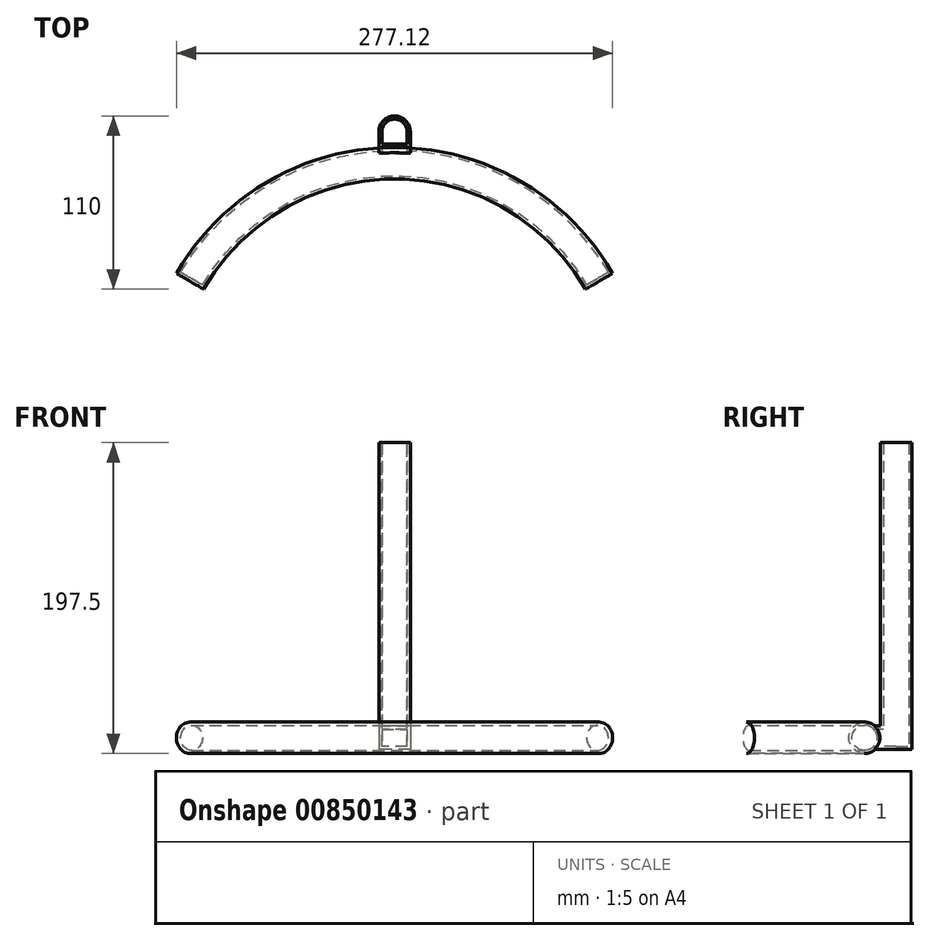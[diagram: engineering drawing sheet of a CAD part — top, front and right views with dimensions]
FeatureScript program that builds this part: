
annotation { "Feature Type Name" : "Feature", "Feature Type Description" : "" }
export const myFeature = defineFeature(function(context is Context, id is Id, definition is map)
    precondition{}
    {
        {
            var Q0;
            Q0=qCreatedBy(makeId("Right.planeOp"),FACE);
            var sketch = newSketch(context, id + "F0", { "sketchPlane" : qUnion([Q0])});
            skCircle(sketch, "E0", {"center": v(0, 0) * mm, "radius": 10 * mm});
            skLineSegment(sketch, "E1", {"start": v(-150, 26.36) * mm, "end": v(-150, -31.35) * mm});
            skSolve(sketch);
        }
        {
            var Q0;
            Q0=makeQuery(id+"F0.imprint","IMPRINT",FACE,{"disambiguationData":[TD([[makeQuery(id+"F0.imprint","IMPRINT",EDGE,{"derivedFrom":sQuery(id+"F0.wireOp",EDGE,"E0")}),1.0]])]});
            var Q1;
            Q1=sQuery(id+"F0.wireOp",EDGE,"E1");
            revolve(context, id + "F1", {"surfaceOperationType" : NewSurfaceOperationType.NEW, "entities" : qUnion([Q0]), "axis" : qUnion([Q1]), "revolveType" : RevolveType.SYMMETRIC, "angle" : 120 * degree});
        }
        {
            var Q0;
            Q0=qCreatedBy(makeId("Front.planeOp"),FACE);
            var sketch = newSketch(context, id + "F2", { "sketchPlane" : qUnion([Q0])});
            skLineSegment(sketch, "E2.bottom", {"start": v(10, 7.5) * mm, "end": v(-10, 7.5) * mm});
            skLineSegment(sketch, "E2.top", {"start": v(10, -7.5) * mm, "end": v(-10, -7.5) * mm});
            skLineSegment(sketch, "E2.left", {"start": v(10, 7.5) * mm, "end": v(10, -7.5) * mm});
            skLineSegment(sketch, "E2.right", {"start": v(-10, 7.5) * mm, "end": v(-10, -7.5) * mm});
            skSolve(sketch);
        }
        {
            var Q0;
            Q0 = qSketchRegion(id + "F2", true);
            extrude(context, id + "F3", {"entities" : qUnion([Q0]), "operationType" : NewBodyOperationType.ADD, "oppositeDirection" : true, "depth" : 30 * mm, "offsetDistance" : 25 * mm});
        }
        {
            var Q0;
            Q0=makeQuery(id+"F3.opExtrude","SWEPT_FACE",FACE,{"disambiguationData":[OSD([sQuery(id+"F2.wireOp",EDGE,"E2.bottom")])]});
            var sketch = newSketch(context, id + "F4", { "sketchPlane" : qUnion([Q0])});
            skLineSegment(sketch, "E3.bottom", {"start": v(-10, 30) * mm, "end": v(10, 30) * mm});
            skLineSegment(sketch, "E3.top", {"start": v(-10, 10) * mm, "end": v(10, 10) * mm});
            skLineSegment(sketch, "E3.left", {"start": v(-10, 30) * mm, "end": v(-10, 10) * mm});
            skLineSegment(sketch, "E3.right", {"start": v(10, 30) * mm, "end": v(10, 10) * mm});
            skSolve(sketch);
        }
        {
            var Q0;
            Q0=makeQuery(id+"F4.imprint","IMPRINT",FACE,{"disambiguationData":[TD([[makeQuery(id+"F4.imprint","IMPRINT",EDGE,{"derivedFrom":sQuery(id+"F4.wireOp",EDGE,"E3.bottom")}),1.0]])]});
            extrude(context, id + "F5", {"entities" : qUnion([Q0]), "operationType" : NewBodyOperationType.ADD, "depth" : 180 * mm, "offsetDistance" : 25 * mm});
        }
        {
            var Q0;
            Q0=makeQuery(id+"F5.boolean.opBoolean","MERGE",EDGE,{"derivedFrom":[makeQuery(id+"F3.opExtrude","CAP_EDGE",EDGE,{"disambiguationData":[OSD([sQuery(id+"F2.wireOp",EDGE,"E2.left")])],"isStart":false}),makeQuery(id+"F5.opExtrude","SWEPT_EDGE",EDGE,{"disambiguationData":[OSD([sQuery(id+"F4.wireOp",EDGE,"E3.bottom"),sQuery(id+"F4.wireOp",EDGE,"E3.right")])]})]});
            var Q1;
            Q1=makeQuery(id+"F5.boolean.opBoolean","MERGE",EDGE,{"derivedFrom":[makeQuery(id+"F3.opExtrude","CAP_EDGE",EDGE,{"disambiguationData":[OSD([sQuery(id+"F2.wireOp",EDGE,"E2.right")])],"isStart":false}),makeQuery(id+"F5.opExtrude","SWEPT_EDGE",EDGE,{"disambiguationData":[OSD([sQuery(id+"F4.wireOp",EDGE,"E3.bottom"),sQuery(id+"F4.wireOp",EDGE,"E3.left")])]})]});
            fillet(context, id + "F6", {"entities" : qUnion([Q0, Q1]), "radius" : 10 * mm, "tangentPropagation" : true, "allowEdgeOverflow" : false});
        }
        {
            var Q0;
            Q0=makeQuery(id+"F5.opExtrude","CAP_FACE",FACE,{"disambiguationData":[OSD([sQuery(id+"F4.wireOp",EDGE,"E3.bottom"),sQuery(id+"F4.wireOp",EDGE,"E3.top"),sQuery(id+"F4.wireOp",EDGE,"E3.left"),sQuery(id+"F4.wireOp",EDGE,"E3.right")])],"isStart":false});
            shell(context, id + "F7", {"entities" : qUnion([Q0]), "thickness" : 2 * mm});
        }
    });
